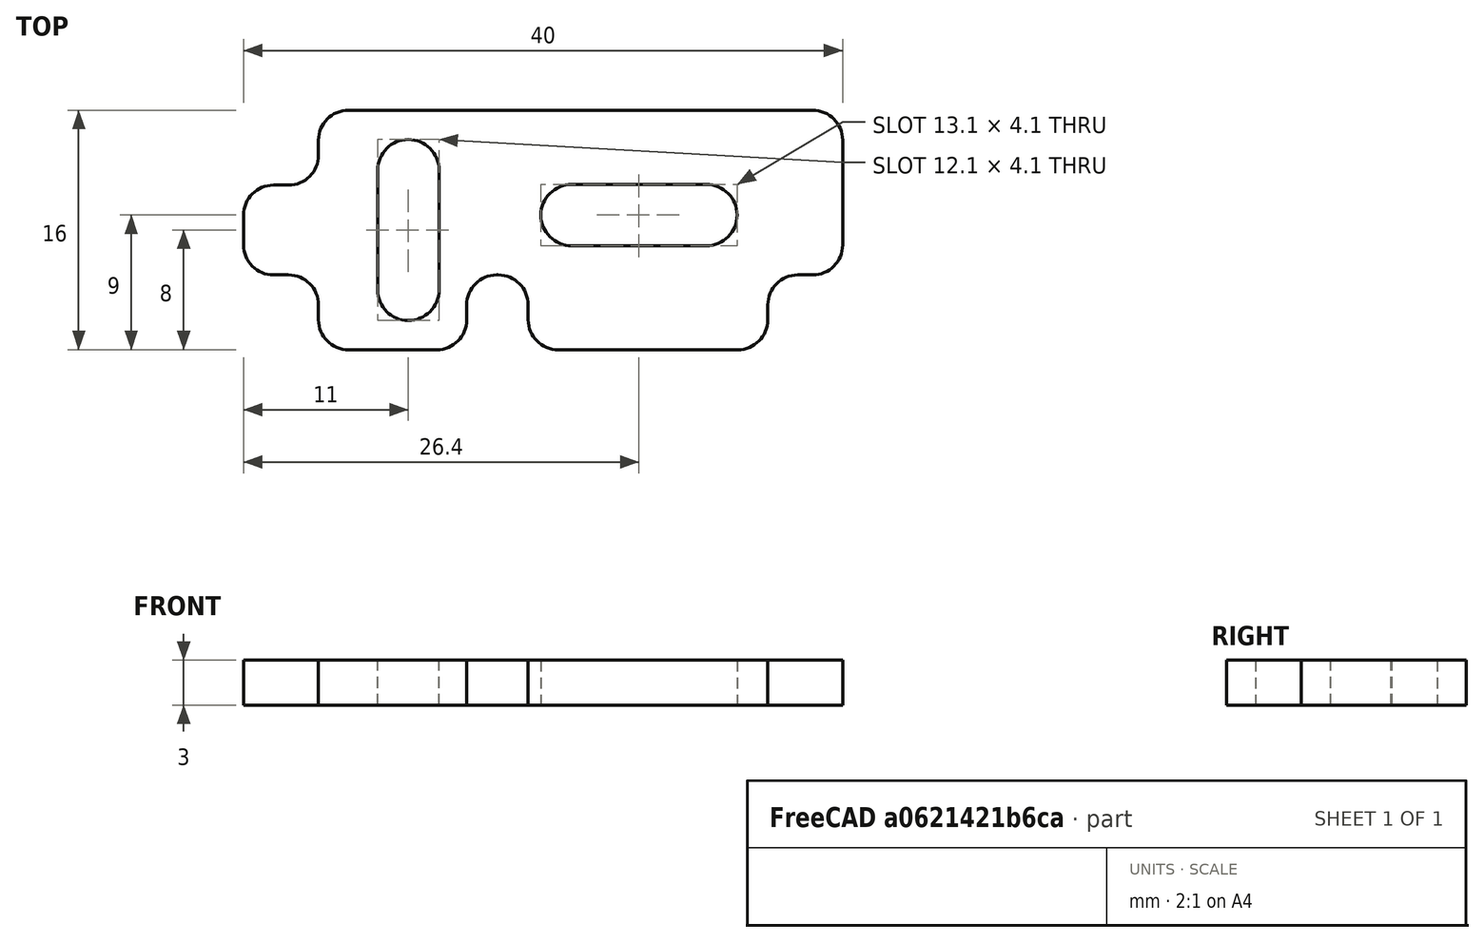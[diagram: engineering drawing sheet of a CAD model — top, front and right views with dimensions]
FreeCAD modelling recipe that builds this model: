
FCSTD DOCUMENT  (FreeCAD 0.19R18614 (Git))
Label: endstop pad
License: All rights reserved
LicenseURL: http://en.wikipedia.org/wiki/All_rights_reserved
objects: Sketcher::SketchObject×1, PartDesign::Pad×1, PartDesign::Body×1, App::Part×1
note: 4 computed .brp shape members not serialized (recipe doc carries the construction recipe); baked Part::Feature solids carry a one-line shape summary decoded from their .brp

FEATURE [Sketcher::SketchObject] Sketch
  MapMode = 5
  Support = -> [XY_Plane001]
  sketch-geometry (36):
    g0: LineSegment StartX=7 StartY=0 StartZ=0 EndX=12.9 EndY=0 EndZ=0
    g1: LineSegment StartX=40 StartY=7 StartZ=0 EndX=40 EndY=14 EndZ=0
    g2: LineSegment StartX=38 StartY=16 StartZ=0 EndX=7 EndY=16 EndZ=0
    g3: LineSegment StartX=0 StartY=9 StartZ=0 EndX=0 EndY=7 EndZ=0
    g4: ArcOfCircle CenterX=21.9 CenterY=9 CenterZ=0 NormalX=0 NormalY=0 NormalZ=1 AngleXU=0 Radius=2.05 StartAngle=1.5708 EndAngle=4.71239
    g5: ArcOfCircle CenterX=30.9 CenterY=9 CenterZ=0 NormalX=0 NormalY=0 NormalZ=1 AngleXU=0 Radius=2.05 StartAngle=4.71239 EndAngle=7.85398
    g6: LineSegment StartX=21.9 StartY=6.95 StartZ=0 EndX=30.9 EndY=6.95 EndZ=0
    g7: LineSegment StartX=21.9 StartY=11.05 StartZ=0 EndX=30.9 EndY=11.05 EndZ=0
    g8: ArcOfCircle CenterX=11 CenterY=12 CenterZ=0 NormalX=0 NormalY=0 NormalZ=1 AngleXU=0 Radius=2.05 StartAngle=1.682e-13 EndAngle=3.14159
    g9: ArcOfCircle CenterX=11 CenterY=4 CenterZ=0 NormalX=0 NormalY=0 NormalZ=1 AngleXU=0 Radius=2.05 StartAngle=3.14159 EndAngle=6.28319
    g10: LineSegment StartX=8.95 StartY=12 StartZ=0 EndX=8.95 EndY=4 EndZ=0
    g11: LineSegment StartX=13.05 StartY=12 StartZ=0 EndX=13.05 EndY=4 EndZ=0
    g12: LineSegment StartX=16.9 StartY=5 StartZ=0 EndX=17 EndY=5 EndZ=0
    g13: LineSegment StartX=19 StartY=3 StartZ=0 EndX=19 EndY=2 EndZ=0
    g14: LineSegment StartX=14.9 StartY=2 StartZ=0 EndX=14.9 EndY=3 EndZ=0
    g15: LineSegment StartX=37 StartY=5 StartZ=0 EndX=38 EndY=5 EndZ=0
    g16: LineSegment StartX=35 StartY=2 StartZ=0 EndX=35 EndY=3 EndZ=0
    g17: LineSegment StartX=3 StartY=5 StartZ=0 EndX=2 EndY=5 EndZ=0
    g18: LineSegment StartX=5 StartY=2 StartZ=0 EndX=5 EndY=3 EndZ=0
    g19: LineSegment StartX=3 StartY=11 StartZ=0 EndX=2 EndY=11 EndZ=0
    g20: LineSegment StartX=5 StartY=14 StartZ=0 EndX=5 EndY=13 EndZ=0
    g21: ArcOfCircle CenterX=7 CenterY=2 CenterZ=0 NormalX=0 NormalY=0 NormalZ=1 AngleXU=0 Radius=2 StartAngle=3.14159 EndAngle=4.71239
    g22: ArcOfCircle CenterX=2 CenterY=7 CenterZ=0 NormalX=0 NormalY=0 NormalZ=1 AngleXU=0 Radius=2 StartAngle=3.14159 EndAngle=4.71239
    g23: ArcOfCircle CenterX=3 CenterY=3 CenterZ=0 NormalX=0 NormalY=0 NormalZ=1 AngleXU=0 Radius=2 StartAngle=0 EndAngle=1.5708
    g24: ArcOfCircle CenterX=2 CenterY=9 CenterZ=0 NormalX=0 NormalY=0 NormalZ=1 AngleXU=0 Radius=2 StartAngle=1.5708 EndAngle=3.14159
    g25: ArcOfCircle CenterX=3 CenterY=13 CenterZ=0 NormalX=0 NormalY=0 NormalZ=1 AngleXU=0 Radius=2 StartAngle=4.71239 EndAngle=6.28319
    g26: ArcOfCircle CenterX=7 CenterY=14 CenterZ=0 NormalX=0 NormalY=0 NormalZ=1 AngleXU=0 Radius=2 StartAngle=1.5708 EndAngle=3.14159
    g27: LineSegment StartX=21 StartY=0 StartZ=0 EndX=33 EndY=0 EndZ=0
    g28: ArcOfCircle CenterX=21 CenterY=2 CenterZ=0 NormalX=0 NormalY=0 NormalZ=1 AngleXU=0 Radius=2 StartAngle=3.14159 EndAngle=4.71239
    g29: ArcOfCircle CenterX=17 CenterY=3 CenterZ=0 NormalX=0 NormalY=0 NormalZ=1 AngleXU=0 Radius=2 StartAngle=0 EndAngle=1.5708
    g30: ArcOfCircle CenterX=16.9 CenterY=3 CenterZ=0 NormalX=0 NormalY=0 NormalZ=1 AngleXU=0 Radius=2 StartAngle=1.5708 EndAngle=3.14159
    g31: ArcOfCircle CenterX=12.9 CenterY=2 CenterZ=0 NormalX=0 NormalY=0 NormalZ=1 AngleXU=0 Radius=2 StartAngle=4.71239 EndAngle=6.28319
    g32: ArcOfCircle CenterX=33 CenterY=2 CenterZ=0 NormalX=0 NormalY=0 NormalZ=1 AngleXU=0 Radius=2 StartAngle=4.71239 EndAngle=6.28319
    g33: ArcOfCircle CenterX=37 CenterY=3 CenterZ=0 NormalX=0 NormalY=0 NormalZ=1 AngleXU=0 Radius=2 StartAngle=1.5708 EndAngle=3.14159
    g34: ArcOfCircle CenterX=38 CenterY=7 CenterZ=0 NormalX=0 NormalY=0 NormalZ=1 AngleXU=0 Radius=2 StartAngle=4.71239 EndAngle=6.28319
    g35: ArcOfCircle CenterX=38 CenterY=14 CenterZ=0 NormalX=0 NormalY=0 NormalZ=1 AngleXU=0 Radius=2 StartAngle=0 EndAngle=1.5708
  constraints (89):
    c: Horizontal(g0)
    c: Horizontal(g2)
    c: Vertical(g1)
    c: Vertical(g3)
    c: Tangent(g4,g7) = 1.5708
    c: Tangent(g4,g6) = -1.5708
    c: Tangent(g6,g5) = -1.5708
    c: Tangent(g7,g5) = 1.5708
    c: Horizontal(g6)
    c: Equal(g4,g5)
    c: Tangent(g8,g11) = 1.5708
    c: Tangent(g8,g10) = -1.5708
    c: Tangent(g10,g9) = -1.5708
    c: Tangent(g11,g9) = 1.5708
    c: Vertical(g10)
    c: Equal(g8,g9)
    c: Horizontal(g12)
    c: Vertical(g13)
    c: Vertical(g14)
    c: Horizontal(g15)
    c: Vertical(g16)
    c: Horizontal(g17)
    c: Vertical(g18)
    c: Horizontal(g19)
    c: Vertical(g20)
    c: Tangent(g0,g21) = -1.5708
    c: Tangent(g18,g21) = 1.5708
    c: Tangent(g17,g22) = 1.5708
    c: Tangent(g3,g22) = -1.5708
    c: Tangent(g17,g23) = -1.5708
    c: Tangent(g18,g23) = -1.5708
    c: Tangent(g3,g24) = -1.5708
    c: Tangent(g19,g24) = -1.5708
    c: Tangent(g19,g25) = 1.5708
    c: Tangent(g20,g25) = 1.5708
    c: Tangent(g2,g26) = -1.5708
    c: Tangent(g20,g26) = -1.5708
    c: Tangent(g0,g27)
    c: Tangent(g13,g28) = -1.5708
    c: Tangent(g27,g28) = -1.5708
    c: Tangent(g12,g29) = 1.5708
    c: Tangent(g13,g29) = 1.5708
    c: Tangent(g12,g30) = 1.5708
    c: Tangent(g14,g30) = 1.5708
    c: Tangent(g14,g31) = -1.5708
    c: Tangent(g0,g31) = -1.5708
    c: Tangent(g16,g32) = -1.5708
    c: Tangent(g27,g32) = -1.5708
    c: Tangent(g16,g33) = 1.5708
    c: Tangent(g15,g33) = 1.5708
    c: Tangent(g15,g34) = -1.5708
    c: Tangent(g1,g34) = -1.5708
    c: Tangent(g2,g35) = -1.5708
    c: Tangent(g1,g35) = -1.5708
    c: Equal(g25,g24)
    c: Equal(g24,g22)
    c: Equal(g22,g23)
    c: Equal(g23,g21)
    c: Equal(g21,g31)
    c: Equal(g31,g30)
    c: Equal(g30,g29)
    c: Equal(g29,g28)
    c: Equal(g28,g32)
    c: Equal(g32,g33)
    c: Equal(g33,g34)
    c: Equal(g34,g35)
    c: Equal(g35,g26)
    c: Radius(g35) = 2
    c: DistanceX(g14,g13) = 4.1
    c: DistanceX(g8,g8) = 4.1
    c: DistanceY(g5,g5) = 4.1
    c: DistanceX(g4,g5) = 9
    c: DistanceY(g9,g8) = 8
    c: DistanceY(g27,g12) = 5
    c: PointOnObject(g0,g-1)
    c: PointOnObject(g3,g-2)
    c: DistanceY(g27,g2) = 16  'Constraint77'
    c: DistanceY(g19,g2) = 5
    c: DistanceX(g3,g20) = 5
    c: DistanceX(g-1,g18) = 5
    c: DistanceX(g16,g1) = 5
    c: DistanceY(g27,g15) = 5
    c: DistanceX(g3,g8) = 11
    c: DistanceX(g-1,g4) = 21.9
    c: DistanceX(g-1,g1) = 40
    c: DistanceX(g-1,g29) = 17
    c: DistanceY(g-1,g5) = 9
    c: DistanceY(g-1,g17) = 5
    c: DistanceY(g-1,g9) = 4
FEATURE [PartDesign::Pad] Pad
  Length = 3
  Length2 = 100
  Profile = -> Sketch
  Type = 0
FEATURE [PartDesign::Body] Body
  Group = -> [Sketch,Pad]
  Origin = -> Origin001
  Tip = -> Pad
FEATURE [App::Part] Part
  Group = -> [Body]
  Origin = -> Origin
